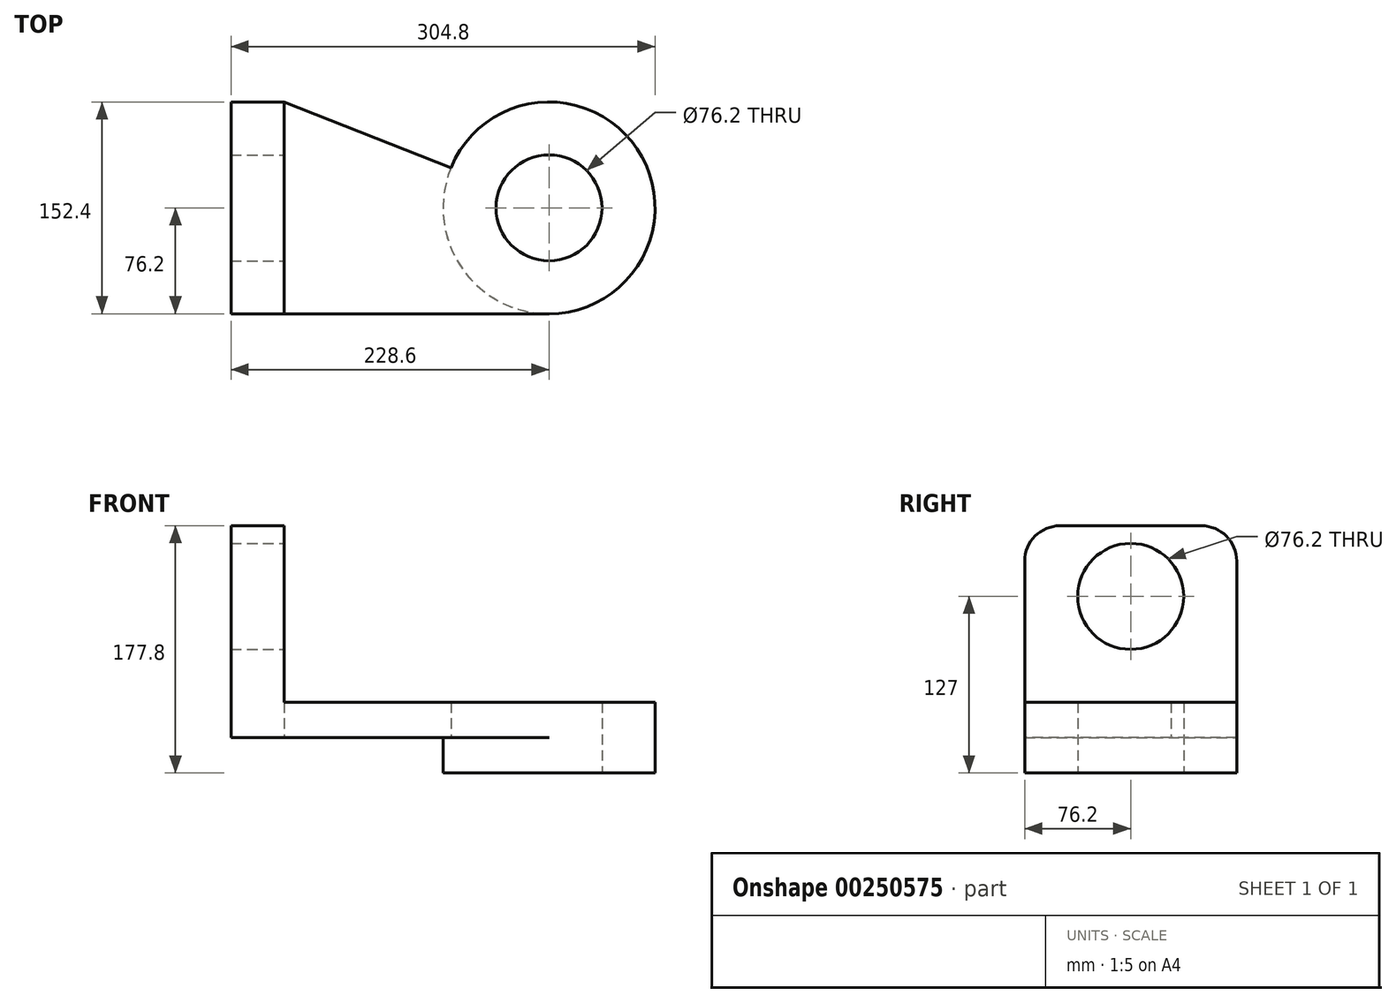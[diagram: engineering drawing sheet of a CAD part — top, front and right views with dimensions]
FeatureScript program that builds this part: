
annotation { "Feature Type Name" : "Feature", "Feature Type Description" : "" }
export const myFeature = defineFeature(function(context is Context, id is Id, definition is map)
    precondition{}
    {
        {
            var Q0;
            Q0=qCreatedBy(makeId("Top.planeOp"),FACE);
            var sketch = newSketch(context, id + "F0", { "sketchPlane" : qUnion([Q0])});
            skCircle(sketch, "E0", {"center": v(0, 0) * mm, "radius": 38.1 * mm});
            skCircle(sketch, "E1", {"center": v(0, 0) * mm, "radius": 76.2 * mm});
            skLineSegment(sketch, "E2", {"start": v(0, -76.2) * mm, "end": v(-190.5, -76.2) * mm});
            skLineSegment(sketch, "E3", {"start": v(-190.5, -76.2) * mm, "end": v(-190.5, 76.2) * mm});
            skLineSegment(sketch, "E4", {"start": v(-190.5, 76.2) * mm, "end": v(-70.51, 28.89) * mm});
            skSolve(sketch);
        }
        {
            var Q0;
            Q0=makeQuery(id+"F0.imprint","IMPRINT",FACE,{"disambiguationData":[TD([[makeQuery(id+"F0.imprint","IMPRINT",EDGE,{"derivedFrom":sQuery(id+"F0.wireOp",EDGE,"E0")}),-1.0]])]});
            var Q1;
            {var subQ0=sQuery(id+"F0.wireOp",EDGE,"E2");Q1=makeQuery(id+"F0.imprint","IMPRINT",FACE,{"disambiguationData":[TD([[makeQuery(id+"F0.imprint","IMPRINT",EDGE,{"derivedFrom":subQ0}),-1.0]])]});}
            extrude(context, id + "F1", {"entities" : qUnion([Q0, Q1]), "depth" : 25.4 * mm});
        }
        {
            var Q0;
            Q0=makeQuery(id+"F1.opExtrude","CAP_FACE",FACE,{"disambiguationData":[OSD([sQuery(id+"F0.wireOp",EDGE,"E0"),sQuery(id+"F0.wireOp",EDGE,"E1"),sQuery(id+"F0.wireOp",EDGE,"E2"),sQuery(id+"F0.wireOp",EDGE,"E3"),sQuery(id+"F0.wireOp",EDGE,"E4")])],"isStart":true});
            var sketch = newSketch(context, id + "F2", { "sketchPlane" : qUnion([Q0])});
            skCircle(sketch, "E5", {"center": v(0, 0) * mm, "radius": 76.2 * mm});
            skCircle(sketch, "E6", {"center": v(0, 0) * mm, "radius": 38.1 * mm});
            skSolve(sketch);
        }
        {
            var Q0;
            {var subQ0=sQuery(id+"F2.wireOp",EDGE,"E5");Q0=makeQuery(id+"F2.imprint","IMPRINT",FACE,{"disambiguationData":[TD([[makeQuery(id+"F2.imprint","IMPRINT",EDGE,{"disambiguationData":[OD(0.0)],"derivedFrom":subQ0}),1.0]])]});}
            extrude(context, id + "F3", {"entities" : qUnion([Q0]), "operationType" : NewBodyOperationType.ADD, "depth" : 25.4 * mm});
        }
        {
            var Q0;
            Q0=makeQuery(id+"F1.opExtrude","SWEPT_FACE",FACE,{"disambiguationData":[OSD([sQuery(id+"F0.wireOp",EDGE,"E3")])]});
            var sketch = newSketch(context, id + "F4", { "sketchPlane" : qUnion([Q0])});
            skLineSegment(sketch, "E7.bottom", {"start": v(76.2, 0) * mm, "end": v(-76.2, 0) * mm});
            skLineSegment(sketch, "E7.top", {"start": v(50.8, 152.4) * mm, "end": v(-50.8, 152.4) * mm});
            skLineSegment(sketch, "E7.left", {"start": v(76.2, 0) * mm, "end": v(76.2, 127) * mm});
            skLineSegment(sketch, "E7.right", {"start": v(-76.2, 0) * mm, "end": v(-76.2, 127) * mm});
            skPoint(sketch, "E8.visualSharp", {"position": v(-76.2, 152.4) * mm});
            skArc(sketch, "E8.filletArc", {"start": v(-50.8, 152.4) * mm, "mid": v(-68.76, 144.96) * mm, "end": v(-76.2, 127) * mm});
            skPoint(sketch, "E9.visualSharp", {"position": v(76.2, 152.4) * mm});
            skArc(sketch, "E9.filletArc", {"start": v(76.2, 127) * mm, "mid": v(68.76, 144.96) * mm, "end": v(50.8, 152.4) * mm});
            skCircle(sketch, "E10", {"center": v(0, 101.6) * mm, "radius": 38.1 * mm});
            skSolve(sketch);
        }
        {
            var Q0;
            Q0 = qSketchRegion(id + "F4", true);
            var Q1;
            Q1=makeQuery(id+"F4.imprint","IMPRINT",FACE,{"disambiguationData":[TD([[makeQuery(id+"F4.imprint","IMPRINT",EDGE,{"derivedFrom":sQuery(id+"F4.wireOp",EDGE,"E7.top")}),1.0]])]});
            extrude(context, id + "F5", {"entities" : qUnion([Q0, Q1]), "operationType" : NewBodyOperationType.ADD, "depth" : 38.1 * mm});
        }
    });
